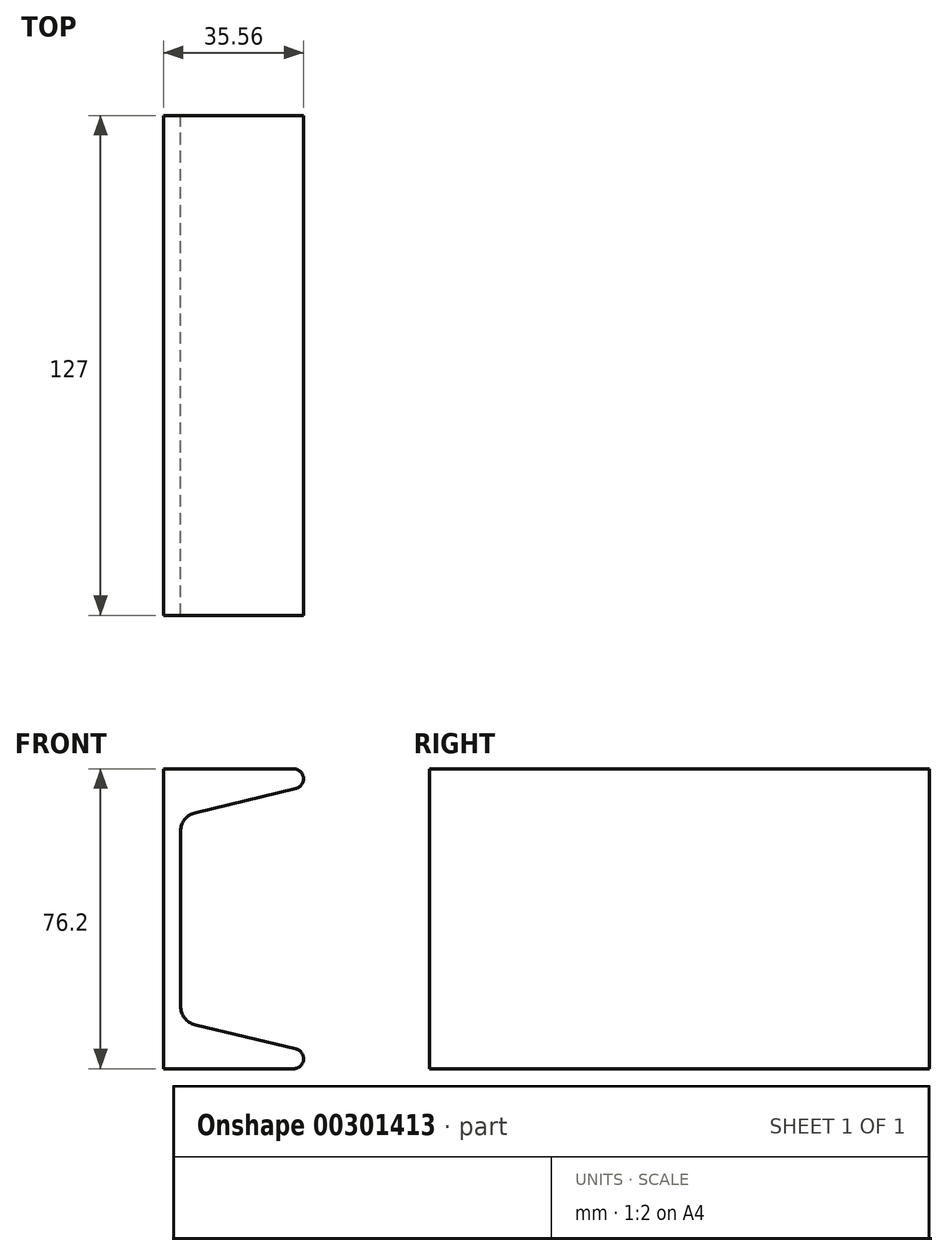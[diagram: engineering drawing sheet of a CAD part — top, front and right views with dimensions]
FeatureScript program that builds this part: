
annotation { "Feature Type Name" : "Feature", "Feature Type Description" : "" }
export const myFeature = defineFeature(function(context is Context, id is Id, definition is map)
    precondition{}
    {
        {
            var Q0;
            Q0=qCreatedBy(makeId("Front.planeOp"),FACE);
            var sketch = newSketch(context, id + "F0", { "sketchPlane" : qUnion([Q0])});
            skLineSegment(sketch, "E0", {"start": v(0, 0) * mm, "end": v(0, 38.1) * mm});
            skLineSegment(sketch, "E1", {"start": v(0, 38.1) * mm, "end": v(33.02, 38.1) * mm});
            skLineSegment(sketch, "E2", {"start": v(33.62, 33.1) * mm, "end": v(8.03, 26.92) * mm});
            skLineSegment(sketch, "E3", {"start": v(4.32, 22.2) * mm, "end": v(4.32, 0) * mm});
            skLineSegment(sketch, "E4.MirrorCS", {"start": v(33.62, -33.1) * mm, "end": v(8.03, -26.92) * mm});
            skLineSegment(sketch, "E5.MirrorCS", {"start": v(0, -38.1) * mm, "end": v(33.02, -38.1) * mm});
            skLineSegment(sketch, "E6.MirrorCS", {"start": v(0, 0) * mm, "end": v(0, -38.1) * mm});
            skLineSegment(sketch, "E7.MirrorCS", {"start": v(4.32, -22.2) * mm, "end": v(4.32, 0) * mm});
            skPoint(sketch, "E8.visualSharp", {"position": v(54.4, -38.1) * mm});
            skArc(sketch, "E8.filletArc", {"start": v(33.02, -38.1) * mm, "mid": v(35.54, -35.86) * mm, "end": v(33.62, -33.1) * mm});
            skPoint(sketch, "E9.visualSharp", {"position": v(54.4, 38.1) * mm});
            skArc(sketch, "E9.filletArc", {"start": v(33.62, 33.1) * mm, "mid": v(35.54, 35.86) * mm, "end": v(33.02, 38.1) * mm});
            skPoint(sketch, "E10.visualSharp", {"position": v(4.32, -26.03) * mm});
            skArc(sketch, "E10.filletArc", {"start": v(4.32, -22.2) * mm, "mid": v(5.36, -25.2) * mm, "end": v(8.03, -26.92) * mm});
            skPoint(sketch, "E11.visualSharp", {"position": v(4.32, 26.03) * mm});
            skArc(sketch, "E11.filletArc", {"start": v(8.03, 26.92) * mm, "mid": v(5.36, 25.2) * mm, "end": v(4.32, 22.2) * mm});
            skSolve(sketch);
        }
        {
            var Q0;
            Q0=makeQuery(id+"F0.imprint","IMPRINT",FACE,{"disambiguationData":[TD([[makeQuery(id+"F0.imprint","IMPRINT",EDGE,{"derivedFrom":sQuery(id+"F0.wireOp",EDGE,"E0")}),-1.0]])]});
            extrude(context, id + "F1", {"entities" : qUnion([Q0]), "endBound" : BoundingType.SYMMETRIC, "depth" : 127 * mm});
        }
    });
